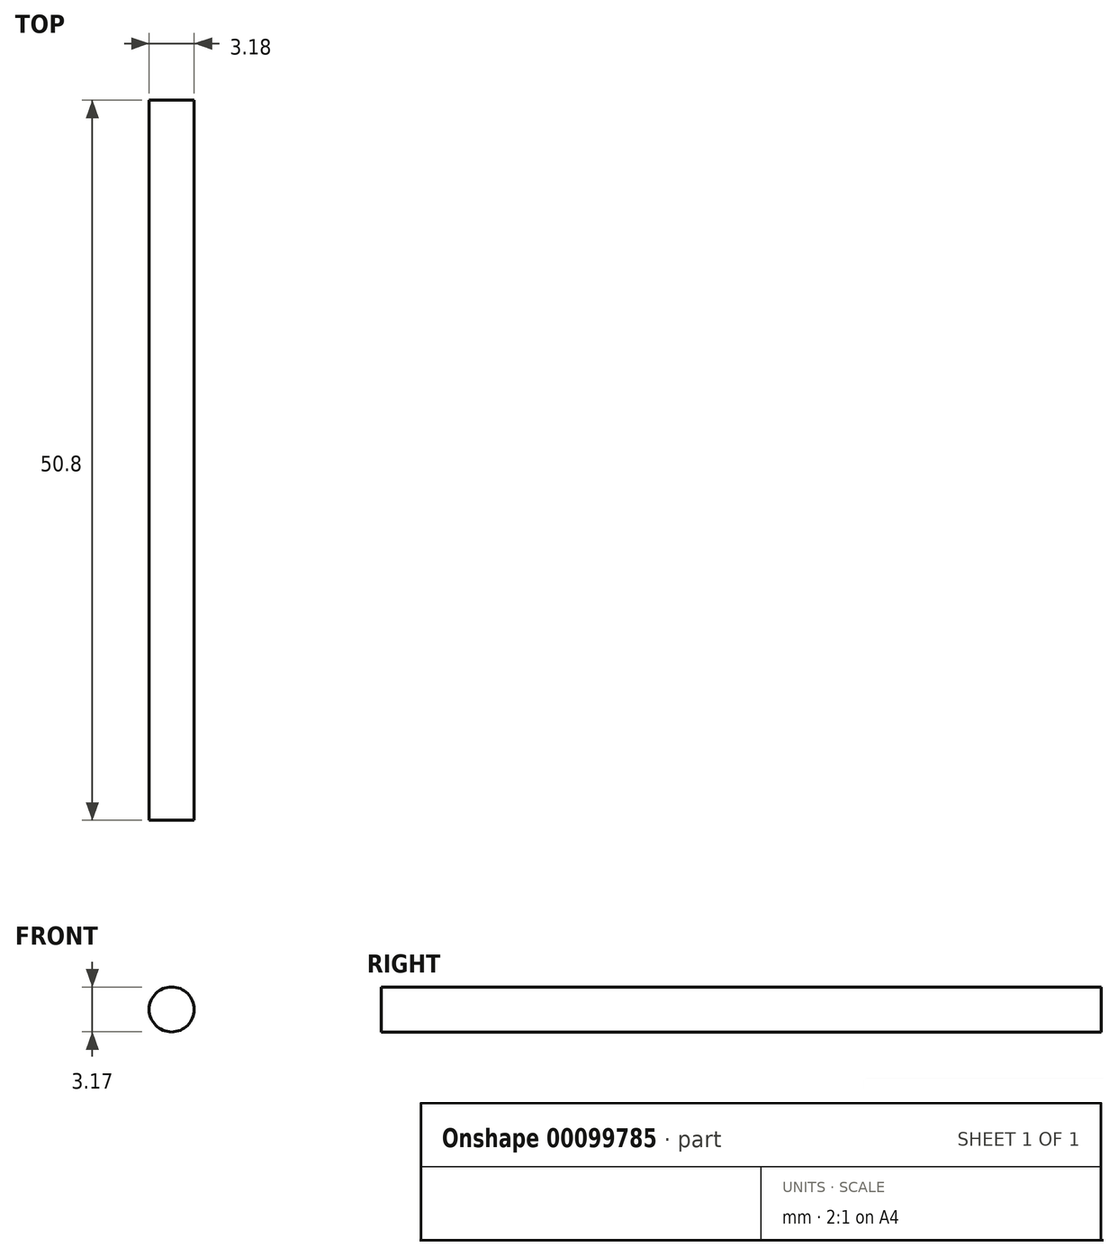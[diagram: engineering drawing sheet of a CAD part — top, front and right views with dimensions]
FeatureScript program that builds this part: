
annotation { "Feature Type Name" : "Feature", "Feature Type Description" : "" }
export const myFeature = defineFeature(function(context is Context, id is Id, definition is map)
    precondition{}
    {
        {
            var Q0;
            Q0=qCreatedBy(makeId("Front.planeOp"),FACE);
            var sketch = newSketch(context, id + "F0", { "sketchPlane" : qUnion([Q0])});
            skCircle(sketch, "E0", {"center": v(0, 0) * mm, "radius": 0.26 * mm});
            skCircle(sketch, "E1", {"center": v(-7.63, 5.55) * mm, "radius": 1.59 * mm});
            skSolve(sketch);
        }
        {
            var Q0;
            Q0=makeQuery(id+"F0.imprint","IMPRINT",FACE,{"disambiguationData":[TD([[makeQuery(id+"F0.imprint","IMPRINT",EDGE,{"derivedFrom":sQuery(id+"F0.wireOp",EDGE,"E1")}),1.0]])]});
            extrude(context, id + "F1", {"entities" : qUnion([Q0]), "depth" : 50.8 * mm});
        }
    });
